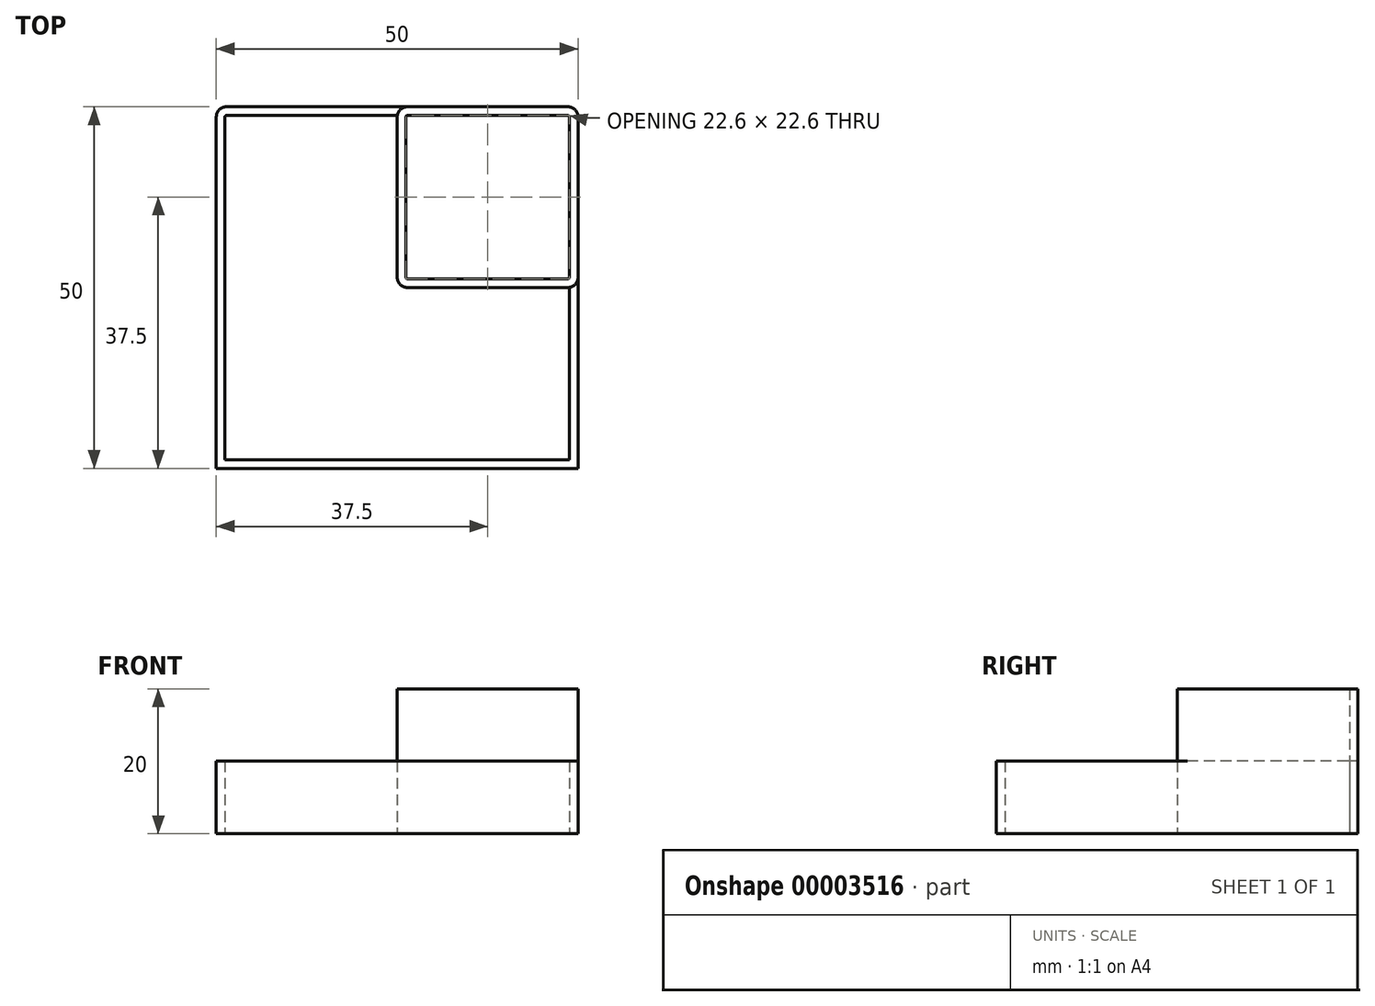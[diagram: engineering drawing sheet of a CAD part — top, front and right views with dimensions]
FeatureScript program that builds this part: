
annotation { "Feature Type Name" : "Feature", "Feature Type Description" : "" }
export const myFeature = defineFeature(function(context is Context, id is Id, definition is map)
    precondition{}
    {
        {
            var Q0;
            Q0=qCreatedBy(makeId("Top.planeOp"),FACE);
            var sketch = newSketch(context, id + "F0", { "sketchPlane" : qUnion([Q0])});
            skLineSegment(sketch, "E0.rect.bottom", {"start": v(23.6, 25) * mm, "end": v(-23.6, 25) * mm});
            skLineSegment(sketch, "E0.rect.top", {"start": v(25, -25) * mm, "end": v(-25, -25) * mm});
            skLineSegment(sketch, "E0.rect.left", {"start": v(25, 23.6) * mm, "end": v(25, -25) * mm});
            skLineSegment(sketch, "E0.rect.right", {"start": v(-25, 23.6) * mm, "end": v(-25, -25) * mm});
            skPoint(sketch, "E0.rect.middle", {"position": v(0, 0) * mm});
            skLineSegment(sketch, "E1.top", {"start": v(23.6, 0) * mm, "end": v(1.4, 0) * mm});
            skLineSegment(sketch, "E1.right", {"start": v(0, 23.6) * mm, "end": v(0, 1.4) * mm});
            skPoint(sketch, "E2.visualSharp", {"position": v(-25, 25) * mm});
            skArc(sketch, "E2.filletArc", {"start": v(-23.6, 25) * mm, "mid": v(-24.59, 24.59) * mm, "end": v(-25, 23.6) * mm});
            skPoint(sketch, "E3.visualSharp", {"position": v(25, 25) * mm});
            skArc(sketch, "E3.filletArc", {"start": v(25, 23.6) * mm, "mid": v(24.59, 24.59) * mm, "end": v(23.6, 25) * mm});
            skLineSegment(sketch, "E4.0", {"start": v(23.8, 23.6) * mm, "end": v(23.8, 1.4) * mm});
            skLineSegment(sketch, "E4.1", {"start": v(23.8, -23.8) * mm, "end": v(-23.8, -23.8) * mm});
            skLineSegment(sketch, "E4.2", {"start": v(-23.8, 23.6) * mm, "end": v(-23.8, -23.8) * mm});
            skLineSegment(sketch, "E5.0", {"start": v(23.6, 23.8) * mm, "end": v(1.4, 23.8) * mm});
            skArc(sketch, "E6", {"start": v(-23.6, 23.8) * mm, "mid": v(-23.74, 23.74) * mm, "end": v(-23.8, 23.6) * mm});
            skArc(sketch, "E7", {"start": v(23.6, 23.8) * mm, "mid": v(23.74, 23.74) * mm, "end": v(23.8, 23.6) * mm});
            skLineSegment(sketch, "E8.0", {"start": v(23.6, 1.2) * mm, "end": v(1.4, 1.2) * mm});
            skLineSegment(sketch, "E8.1", {"start": v(1.2, 23.6) * mm, "end": v(1.2, 1.4) * mm});
            skLineSegment(sketch, "E9.trimOffspring", {"start": v(-0.2, 23.8) * mm, "end": v(-23.6, 23.8) * mm});
            skLineSegment(sketch, "E10.trimOffspring", {"start": v(23.8, -0.2) * mm, "end": v(23.8, -23.8) * mm});
            skArc(sketch, "E11.filletArc", {"start": v(0, 1.4) * mm, "mid": v(0.41, 0.41) * mm, "end": v(1.4, 0) * mm});
            skPoint(sketch, "E12.visualSharp", {"position": v(1.2, 23.8) * mm});
            skArc(sketch, "E12.filletArc", {"start": v(1.4, 23.8) * mm, "mid": v(1.26, 23.74) * mm, "end": v(1.2, 23.6) * mm});
            skPoint(sketch, "E13.visualSharp", {"position": v(0, 23.8) * mm});
            skArc(sketch, "E13.filletArc", {"start": v(0, 23.6) * mm, "mid": v(-0.06, 23.74) * mm, "end": v(-0.2, 23.8) * mm});
            skPoint(sketch, "E14.visualSharp", {"position": v(23.8, 1.2) * mm});
            skArc(sketch, "E14.filletArc", {"start": v(23.6, 1.2) * mm, "mid": v(23.74, 1.26) * mm, "end": v(23.8, 1.4) * mm});
            skPoint(sketch, "E15.visualSharp", {"position": v(23.8, 0) * mm});
            skArc(sketch, "E15.filletArc", {"start": v(23.8, -0.2) * mm, "mid": v(23.74, -0.06) * mm, "end": v(23.6, 0) * mm});
            skPoint(sketch, "E16.visualSharp", {"position": v(1.2, 1.2) * mm});
            skArc(sketch, "E16.filletArc", {"start": v(1.2, 1.4) * mm, "mid": v(1.26, 1.26) * mm, "end": v(1.4, 1.2) * mm});
            skSolve(sketch);
        }
        {
            var Q0;
            Q0 = qSketchRegion(id + "F0", true);
            extrude(context, id + "F1", {"entities" : qUnion([Q0]), "depth" : 10 * mm});
        }
        {
            var Q0;
            Q0=makeQuery(id+"F1.opExtrude","CAP_FACE",FACE,{"disambiguationData":[OSD([sQuery(id+"F0.wireOp",EDGE,"E0.rect.bottom"),sQuery(id+"F0.wireOp",EDGE,"E0.rect.top"),sQuery(id+"F0.wireOp",EDGE,"E0.rect.left"),sQuery(id+"F0.wireOp",EDGE,"E0.rect.right"),sQuery(id+"F0.wireOp",EDGE,"E1.top"),sQuery(id+"F0.wireOp",EDGE,"E1.right"),sQuery(id+"F0.wireOp",EDGE,"E2.filletArc"),sQuery(id+"F0.wireOp",EDGE,"E3.filletArc"),sQuery(id+"F0.wireOp",EDGE,"E4.0"),sQuery(id+"F0.wireOp",EDGE,"E4.1"),sQuery(id+"F0.wireOp",EDGE,"E4.2"),sQuery(id+"F0.wireOp",EDGE,"E5.0"),sQuery(id+"F0.wireOp",EDGE,"E6"),sQuery(id+"F0.wireOp",EDGE,"E7"),sQuery(id+"F0.wireOp",EDGE,"E8.0"),sQuery(id+"F0.wireOp",EDGE,"E8.1"),sQuery(id+"F0.wireOp",EDGE,"E9.trimOffspring"),sQuery(id+"F0.wireOp",EDGE,"E10.trimOffspring"),sQuery(id+"F0.wireOp",EDGE,"E11.filletArc"),sQuery(id+"F0.wireOp",EDGE,"23da3eb2-5feb-4a37-a355-33ea29388dd2.0"),sQuery(id+"F0.wireOp",EDGE,"E12.filletArc"),sQuery(id+"F0.wireOp",EDGE,"E13.filletArc"),sQuery(id+"F0.wireOp",EDGE,"E14.filletArc"),sQuery(id+"F0.wireOp",EDGE,"E15.filletArc")])],"isStart":false});
            var sketch = newSketch(context, id + "F2", { "sketchPlane" : qUnion([Q0])});
            skLineSegment(sketch, "E17.bottom", {"start": v(1.4, 25) * mm, "end": v(23.6, 25) * mm});
            skLineSegment(sketch, "E17.top", {"start": v(1.4, 0) * mm, "end": v(23.6, 0) * mm});
            skLineSegment(sketch, "E17.left", {"start": v(0, 23.6) * mm, "end": v(0, 1.4) * mm});
            skLineSegment(sketch, "E17.right", {"start": v(25, 23.6) * mm, "end": v(25, 1.4) * mm});
            skLineSegment(sketch, "E18.bottom", {"start": v(23.6, 1.2) * mm, "end": v(1.4, 1.2) * mm});
            skLineSegment(sketch, "E18.top", {"start": v(23.6, 23.8) * mm, "end": v(1.4, 23.8) * mm});
            skLineSegment(sketch, "E18.left", {"start": v(23.8, 1.4) * mm, "end": v(23.8, 23.6) * mm});
            skLineSegment(sketch, "E18.right", {"start": v(1.2, 1.4) * mm, "end": v(1.2, 23.6) * mm});
            skPoint(sketch, "E19.visualSharp", {"position": v(1.2, 23.8) * mm});
            skArc(sketch, "E19.filletArc", {"start": v(1.4, 23.8) * mm, "mid": v(1.26, 23.74) * mm, "end": v(1.2, 23.6) * mm});
            skPoint(sketch, "E20.visualSharp", {"position": v(1.2, 1.2) * mm});
            skArc(sketch, "E20.filletArc", {"start": v(1.2, 1.4) * mm, "mid": v(1.26, 1.26) * mm, "end": v(1.4, 1.2) * mm});
            skPoint(sketch, "E21.visualSharp", {"position": v(23.8, 1.2) * mm});
            skArc(sketch, "E21.filletArc", {"start": v(23.6, 1.2) * mm, "mid": v(23.74, 1.26) * mm, "end": v(23.8, 1.4) * mm});
            skPoint(sketch, "E22.visualSharp", {"position": v(23.8, 23.8) * mm});
            skArc(sketch, "E22.filletArc", {"start": v(23.8, 23.6) * mm, "mid": v(23.74, 23.74) * mm, "end": v(23.6, 23.8) * mm});
            skPoint(sketch, "E23.visualSharp", {"position": v(0, 25) * mm});
            skArc(sketch, "E23.filletArc", {"start": v(1.4, 25) * mm, "mid": v(0.41, 24.59) * mm, "end": v(0, 23.6) * mm});
            skPoint(sketch, "E24.visualSharp", {"position": v(0, 0) * mm});
            skArc(sketch, "E24.filletArc", {"start": v(0, 1.4) * mm, "mid": v(0.41, 0.41) * mm, "end": v(1.4, 0) * mm});
            skPoint(sketch, "E25.visualSharp", {"position": v(25, 0) * mm});
            skArc(sketch, "E25.filletArc", {"start": v(23.6, 0) * mm, "mid": v(24.59, 0.41) * mm, "end": v(25, 1.4) * mm});
            skPoint(sketch, "E26.visualSharp", {"position": v(25, 25) * mm});
            skArc(sketch, "E26.filletArc", {"start": v(25, 23.6) * mm, "mid": v(24.59, 24.59) * mm, "end": v(23.6, 25) * mm});
            skSolve(sketch);
        }
        {
            var Q0;
            Q0 = qSketchRegion(id + "F2", true);
            extrude(context, id + "F3", {"entities" : qUnion([Q0]), "operationType" : NewBodyOperationType.ADD, "depth" : 10 * mm});
        }
    });
